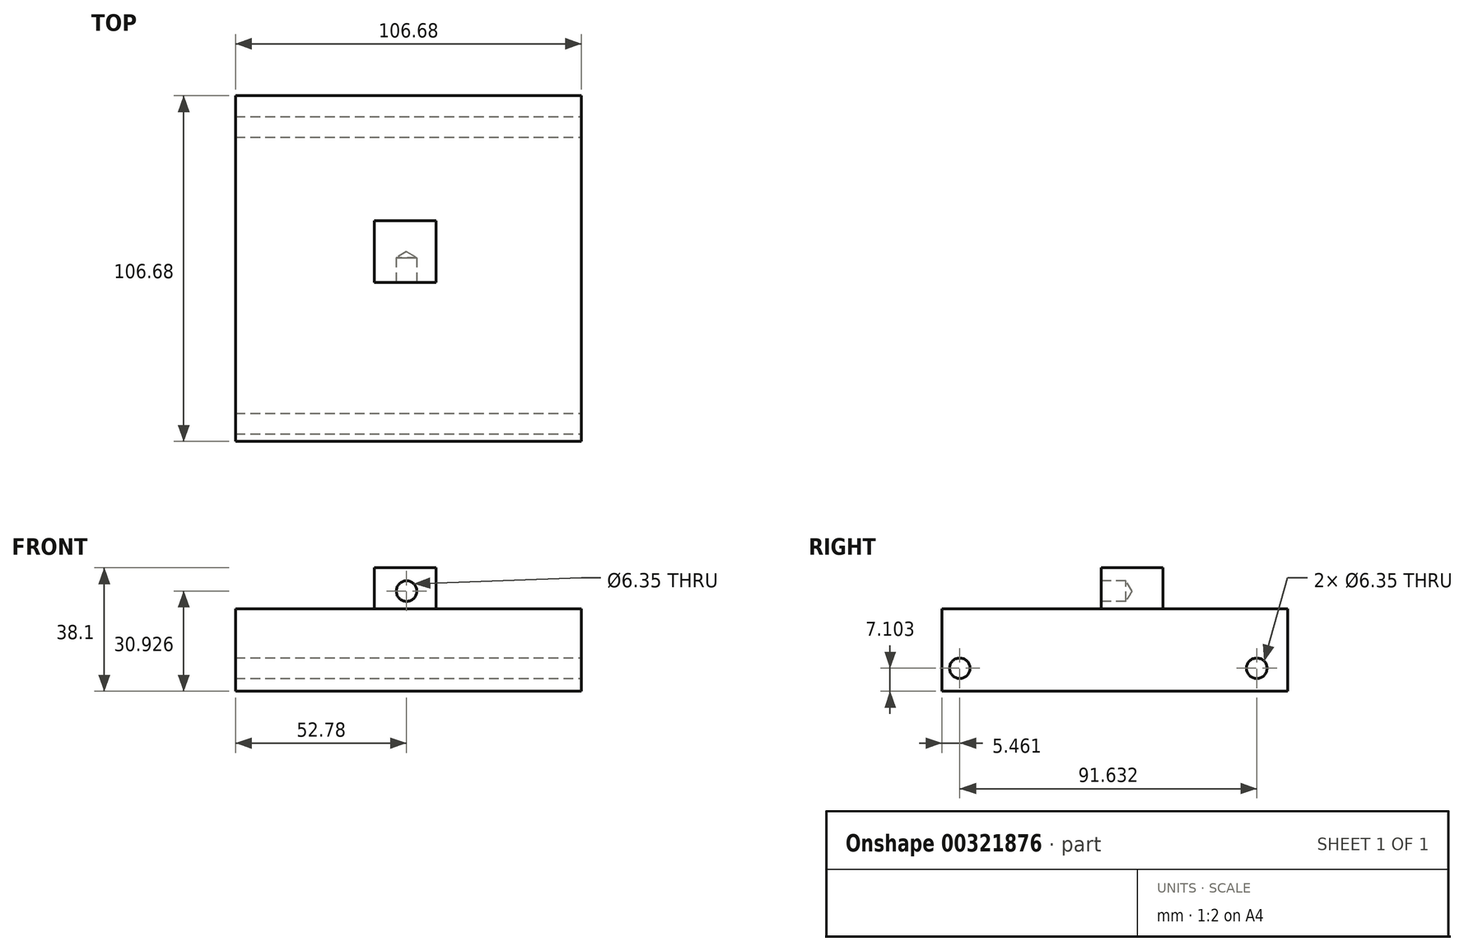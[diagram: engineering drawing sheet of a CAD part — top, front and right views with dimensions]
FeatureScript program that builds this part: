
annotation { "Feature Type Name" : "Feature", "Feature Type Description" : "" }
export const myFeature = defineFeature(function(context is Context, id is Id, definition is map)
    precondition{}
    {
        {
            var Q0;
            Q0=qCreatedBy(makeId("Top.planeOp"),FACE);
            var sketch = newSketch(context, id + "F0", { "sketchPlane" : qUnion([Q0])});
            skLineSegment(sketch, "E0.bottom", {"start": v(-42.84, 57.6) * mm, "end": v(63.84, 57.6) * mm});
            skLineSegment(sketch, "E0.top", {"start": v(-42.84, -49.08) * mm, "end": v(63.84, -49.08) * mm});
            skLineSegment(sketch, "E0.left", {"start": v(-42.84, 57.6) * mm, "end": v(-42.84, -49.08) * mm});
            skLineSegment(sketch, "E0.right", {"start": v(63.84, 57.6) * mm, "end": v(63.84, -49.08) * mm});
            skSolve(sketch);
        }
        {
            var Q0;
            Q0 = qSketchRegion(id + "F0", true);
            extrude(context, id + "F1", {"entities" : qUnion([Q0]), "depth" : 25.4 * mm});
        }
        {
            var Q0;
            Q0=makeQuery(id+"F1.opExtrude","SWEPT_FACE",FACE,{"disambiguationData":[OSD([sQuery(id+"F0.wireOp",EDGE,"E0.right")])]});
            var sketch = newSketch(context, id + "F2", { "sketchPlane" : qUnion([Q0])});
            skPoint(sketch, "E1", {"position": v(-43.62, 7.1) * mm});
            skPoint(sketch, "E2", {"position": v(48.01, 7.1) * mm});
            skSolve(sketch);
        }
        {
            var Q0;
            Q0=sQuery(id+"F2.wireOp",VERTEX,"E1");
            var Q1;
            Q1=sQuery(id+"F2.wireOp",VERTEX,"E2");
            var Q2;
            Q2=makeQuery(id+"F1.opExtrude","SWEPT_BODY",BODY,{"disambiguationData":[OSD([sQuery(id+"F0.wireOp",EDGE,"E0.bottom"),sQuery(id+"F0.wireOp",EDGE,"E0.top"),sQuery(id+"F0.wireOp",EDGE,"E0.left"),sQuery(id+"F0.wireOp",EDGE,"E0.right")])]});
            hole(context, id + "F3", {"style" : HoleStyle.SIMPLE, "endStyle" : HoleEndStyle.THROUGH, "holeDiameter" : 6.35 * mm, "tappedDepth" : 12.7 * mm, "tapClearance" : 3, "locations" : qUnion([Q0, Q1]), "scope" : qUnion([Q2])});
        }
        {
            var Q0;
            Q0=makeQuery(id+"F1.opExtrude","CAP_FACE",FACE,{"disambiguationData":[OSD([sQuery(id+"F0.wireOp",EDGE,"E0.bottom"),sQuery(id+"F0.wireOp",EDGE,"E0.top"),sQuery(id+"F0.wireOp",EDGE,"E0.left"),sQuery(id+"F0.wireOp",EDGE,"E0.right")])],"isStart":false});
            var sketch = newSketch(context, id + "F4", { "sketchPlane" : qUnion([Q0])});
            skLineSegment(sketch, "E3.bottom", {"start": v(0, 0) * mm, "end": v(19.02, 0) * mm});
            skLineSegment(sketch, "E3.top", {"start": v(0, 19.02) * mm, "end": v(19.02, 19.02) * mm});
            skLineSegment(sketch, "E3.left", {"start": v(0, 0) * mm, "end": v(0, 19.02) * mm});
            skLineSegment(sketch, "E3.right", {"start": v(19.02, 0) * mm, "end": v(19.02, 19.02) * mm});
            skSolve(sketch);
        }
        {
            var Q0;
            Q0=makeQuery(id+"F4.imprint","IMPRINT",FACE,{"disambiguationData":[TD([[makeQuery(id+"F4.imprint","IMPRINT",EDGE,{"derivedFrom":sQuery(id+"F4.wireOp",EDGE,"E3.bottom")}),1.0]])]});
            extrude(context, id + "F5", {"entities" : qUnion([Q0]), "operationType" : NewBodyOperationType.ADD, "depth" : 12.7 * mm});
        }
        {
            var Q0;
            Q0=makeQuery(id+"F5.opExtrude","SWEPT_FACE",FACE,{"disambiguationData":[OSD([sQuery(id+"F4.wireOp",EDGE,"E3.bottom")])]});
            var sketch = newSketch(context, id + "F6", { "sketchPlane" : qUnion([Q0])});
            skPoint(sketch, "E4", {"position": v(9.94, 30.93) * mm});
            skSolve(sketch);
        }
        {
            var Q0;
            Q0=sQuery(id+"F6.wireOp",VERTEX,"E4");
            var Q1;
            Q1=makeQuery(id+"F1.opExtrude","SWEPT_BODY",BODY,{"disambiguationData":[OSD([sQuery(id+"F0.wireOp",EDGE,"E0.bottom"),sQuery(id+"F0.wireOp",EDGE,"E0.top"),sQuery(id+"F0.wireOp",EDGE,"E0.left"),sQuery(id+"F0.wireOp",EDGE,"E0.right")])]});
            hole(context, id + "F7", {"style" : HoleStyle.SIMPLE, "endStyle" : HoleEndStyle.BLIND, "holeDiameter" : 6.35 * mm, "holeDepth" : 7.62 * mm, "tappedDepth" : 12.7 * mm, "tapClearance" : 3, "locations" : qUnion([Q0]), "scope" : qUnion([Q1])});
        }
    });
